# Revit family: FAP42T
name_source: partatom
category: Communication Devices
revit_build: Autodesk Revit 2014 (Build: 20140709_2115(x64)
units: mm (PartAtom-declared; Revit-internal decimal feet)

## types (1)
- Two Way, Full Range, Coaxial Ceiling Loudspeaker
    Baffle Material = <By Category>
    Body Material = QF_Metal - Stainless - Polished
    Color = <By Category>
    Cost = 116.99 $
    Cost MSRP = 116.99 $
    Coverage Horizontal = 110.00°
    Coverage Vertical = 110.00°
    Cutout Diameter = 9
    Depth = 10.5 "
    Description = 4" IN-CEILING LOUDSPEAKER WITH 16-WATT 70/100V TRANSFORMER AND PORTED ENCLOSURE - BLACK
    Dispersion Angle = 130.00°
    Enclosure Material = <By Category>
    Family Code (default) = LOUD SPEAKERS
    Frequency Response  = 75Hz - 20kHz
    Grill Material = QF_Plastic - Black - Fine Textured
    HF Driver = Coaxially Mounted PEI Dome Tweeter
    Height = 8.76 "
    Horizontal Symmetry = Yes
    IQ Category = SPEAKERS
    Impedance = 8
    Ingress Protection = IP-21
    Manufacturer = ATLAS SOUND
    Manufacturer URL = www.atlasied.com/","https://www.atlasied.com
    Market = Commercial, Higher Education, Emergency
    MasterFormat = 27 41 13
    MaterFormat Title = SPEAKERS
    Model = FAP42T
    Mount Material = QF_Plastic - White - Smooth
    Mounting/Rigging Provisions = Patented Safety First Mounting System
    OmniClass Number = 23-37 17 13 19
    OmniClass Title = SPEAKERS
    Power Handling = 25
    Power Rating (RMS) = 25 Watts
    Product Documentation Link = www.atlasied.com/f/1799/ATS001159%20FAP42T%20Datasheet%20RevG.pdf
    Product Page URL = www.atlasied.com/fap42t
    Regulatory Compliance = UL Listed to Comply with UL1480, UL2043 and CSA60065. Suitable for Use in Air Handling Spaces per NFPA 70 and NFPA 90
    SPL Max = 107
    Safety Agency Ratings = UL Listed to Comply with UL1480, UL2043 and CSA60065. Suitable for Use in Air Handling Spaces per NFPA 70 and NFPA 90
    Safety Features = 1 Safety Hang Point
    ScheduleType |RF| = AtlasIED Master
    Sensitivity = 88
    Speaker Dispersion = 130.00°
    Speaker Type = S1
    Transformer Option = Yes
    URL = www.atlassound.com
    Vertical Symmetry = Yes
    Warranty = 5 Year
    Weight Dimensional = 22.83
    Width = 10.5 "
    Woofer Impedence = 4" Poly Cone with Butyl Rubber Surround

## geometry (parser evidence)
native form markers: Blend x6, Sweep x2
no freeform markers — native parametric forms only
